# Revit family: Towers
name_source: partatom
category: Furniture
revit_build: Autodesk Revit 2018 (Build: 20181011_1500(x64)
units: mm (PartAtom-declared; Revit-internal decimal feet)

## family parameters
Always vertical = Yes
Cut with Voids When Loaded = No
OmniClass Number = 23.40.20.00
OmniClass Title = General Furniture and Specialties
Room Calculation Point = No
Shared = No
Work Plane-Based = No

## types (2) — shared parameters
Carcass_Material = Steel, Mild
Category = Classics
Colour = Performance range
Door_Material = Steel, Mild
Manufacturer = Bisley
Range = Tower
Revision = V1
Routine Maintenance = We recommend you clean your unit with warm water and a mild detergent solution. A damp cloth can be used to remove dust particles.
URL = www.bisley.com
Uniclass 2015 Code = Pr_40_30_78_57
Uniclass2015Title = 78 - Shelves and Storage Units
Uniclass2015Version = V1.13
Warranty = 10 Years

## per-type parameters (varying)
| type | 4 | Dimensions | Model Reference | Unit Type |
| BTW3BR2S | No | 1118mm x 450mm x 800mm | BTW3BR2S | Yes |
| BTW4BR4S | Yes | 1300mm x 450mm x 800mm | BT4BR4S | No |

## geometry (parser evidence)
native form markers: Sweep x2
no freeform markers — native parametric forms only
